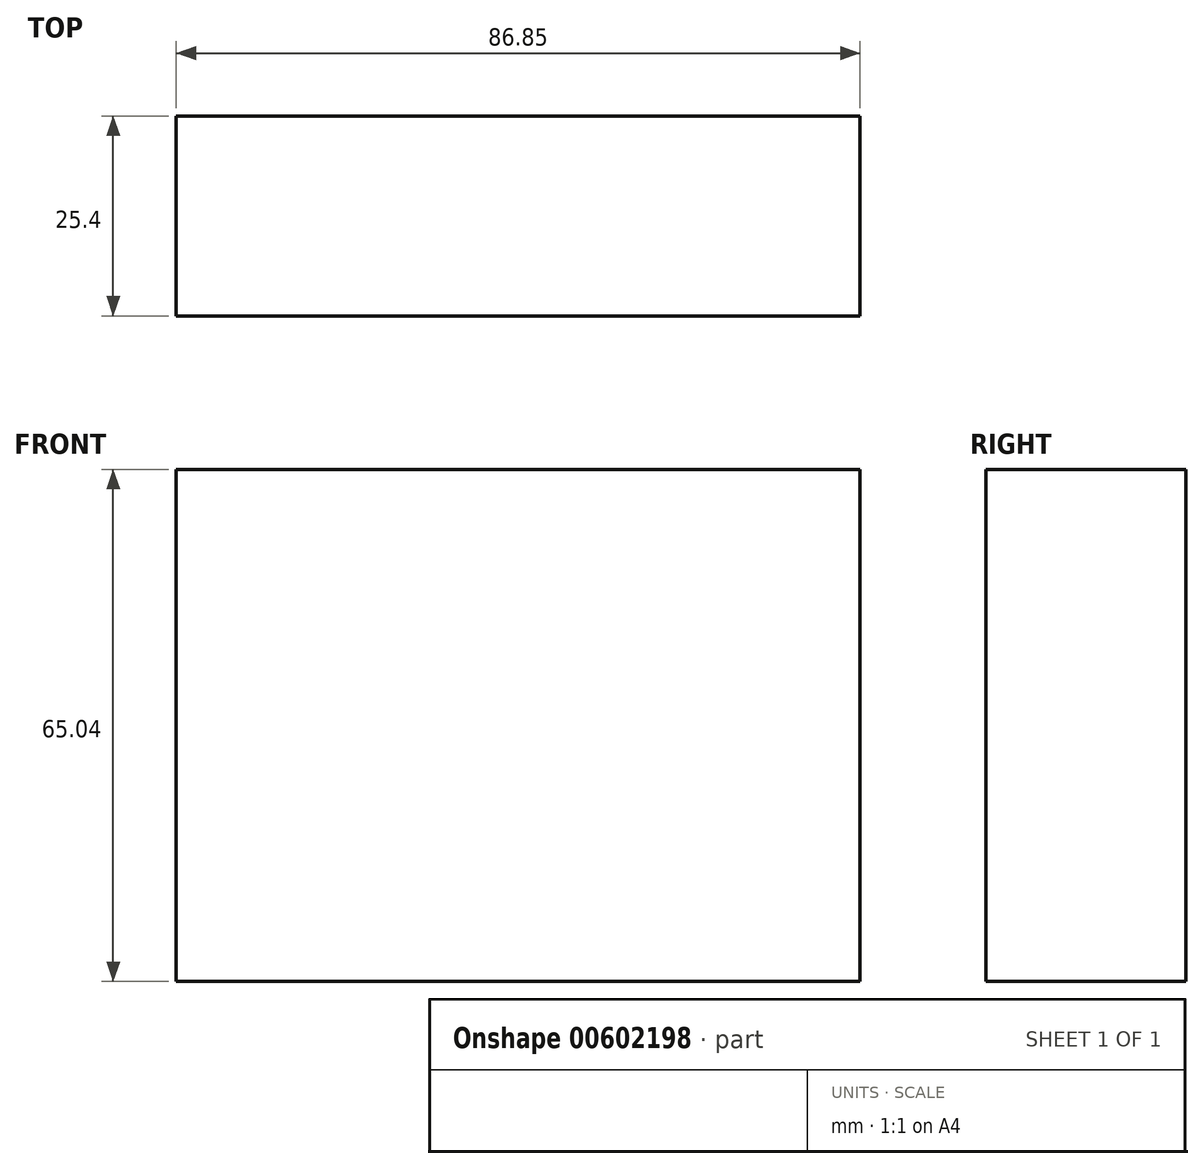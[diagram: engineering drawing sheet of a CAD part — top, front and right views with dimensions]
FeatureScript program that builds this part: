
annotation { "Feature Type Name" : "Feature", "Feature Type Description" : "" }
export const myFeature = defineFeature(function(context is Context, id is Id, definition is map)
    precondition{}
    {
        {
            var Q0;
            Q0=qCreatedBy(makeId("Front.planeOp"),FACE);
            var sketch = newSketch(context, id + "F0", { "sketchPlane" : qUnion([Q0])});
            skLineSegment(sketch, "E0.bottom", {"start": v(-26.24, -38.06) * mm, "end": v(60.6, -38.06) * mm});
            skLineSegment(sketch, "E0.top", {"start": v(-26.24, 26.98) * mm, "end": v(60.6, 26.98) * mm});
            skLineSegment(sketch, "E0.left", {"start": v(-26.24, -38.06) * mm, "end": v(-26.24, 26.98) * mm});
            skLineSegment(sketch, "E0.right", {"start": v(60.6, -38.06) * mm, "end": v(60.6, 26.98) * mm});
            skSolve(sketch);
        }
        {
            var Q0;
            Q0=makeQuery(id+"F0.imprint","IMPRINT",FACE,{"disambiguationData":[TD([[makeQuery(id+"F0.imprint","IMPRINT",EDGE,{"derivedFrom":sQuery(id+"F0.wireOp",EDGE,"E0.bottom")}),1.0]])]});
            extrude(context, id + "F1", {"entities" : qUnion([Q0]), "depth" : 25.4 * mm, "offsetDistance" : 25.4 * mm});
        }
    });
